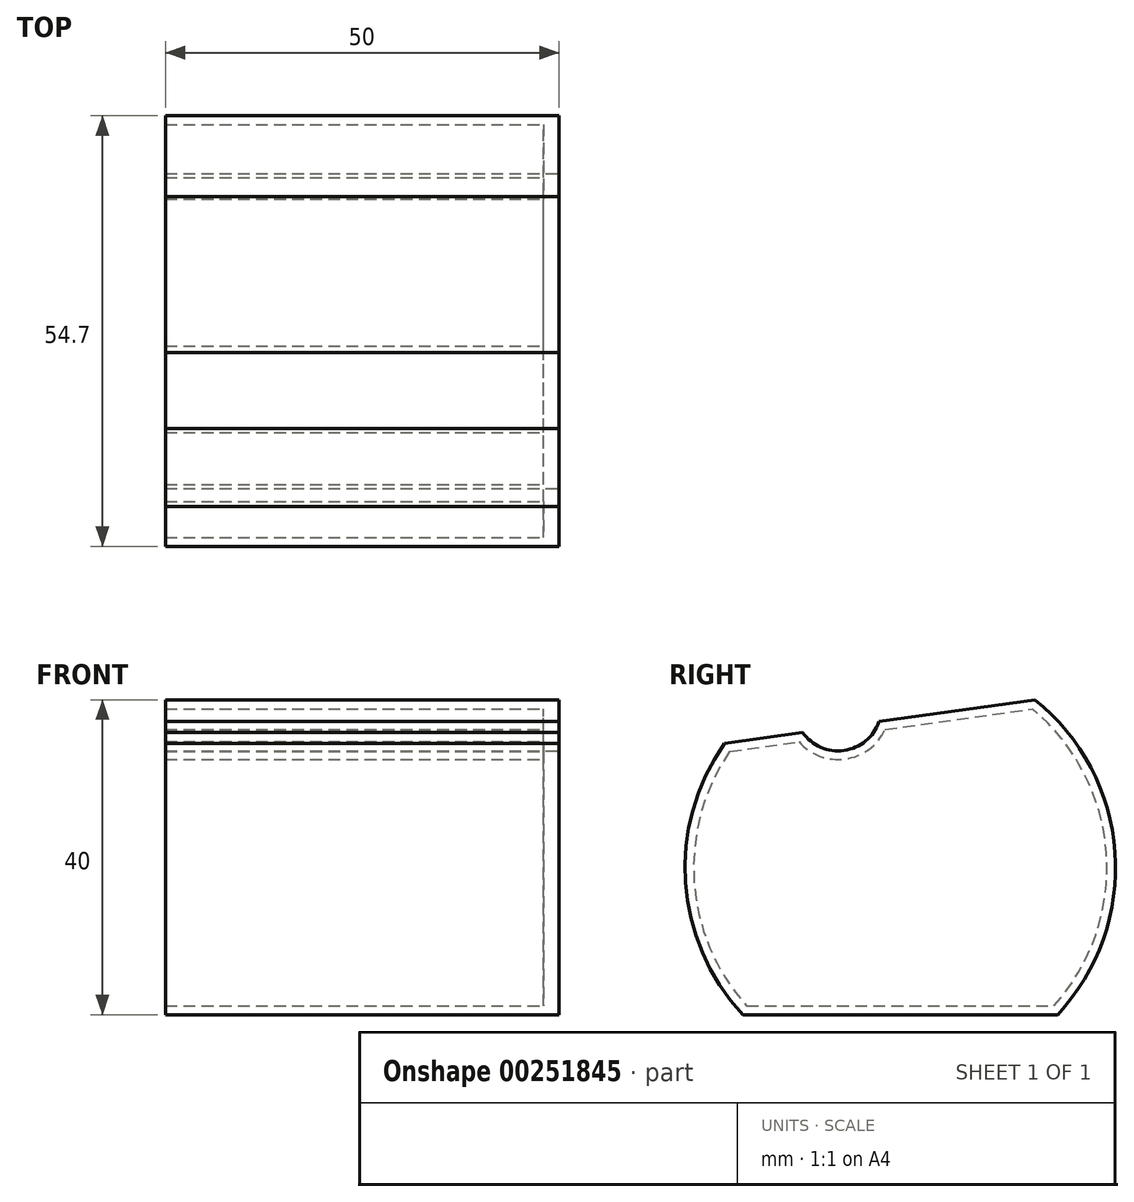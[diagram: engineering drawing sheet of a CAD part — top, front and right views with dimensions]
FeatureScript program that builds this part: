
annotation { "Feature Type Name" : "Feature", "Feature Type Description" : "" }
export const myFeature = defineFeature(function(context is Context, id is Id, definition is map)
    precondition{}
    {
        {
            var Q0;
            Q0=qCreatedBy(makeId("Right.planeOp"),FACE);
            var sketch = newSketch(context, id + "F0", { "sketchPlane" : qUnion([Q0])});
            skArc(sketch, "E0", {"start": v(21.5, -15.89) * mm, "mid": v(28.78, 4.75) * mm, "end": v(18.6, 24.11) * mm});
            skArc(sketch, "E1.trimOffspring", {"start": v(-20.82, 18.58) * mm, "mid": v(-25.79, 0.93) * mm, "end": v(-18.5, -15.89) * mm});
            skLineSegment(sketch, "E2", {"start": v(-20.82, 18.58) * mm, "end": v(-10.91, 19.97) * mm});
            skLineSegment(sketch, "E3.trimOffspring", {"start": v(25.8, -84.09) * mm, "end": v(25.8, -84.09) * mm});
            skLineSegment(sketch, "E4", {"start": v(-18.5, -15.89) * mm, "end": v(21.5, -15.89) * mm});
            skArc(sketch, "E5", {"start": v(-10.91, 19.97) * mm, "mid": v(-5.64, 17.68) * mm, "end": v(-1.21, 21.33) * mm});
            skLineSegment(sketch, "E6.trimOffspring", {"start": v(-1.21, 21.33) * mm, "end": v(18.6, 24.11) * mm});
            skLineSegment(sketch, "E7.0", {"start": v(-20.19, 17.55) * mm, "end": v(-11.39, 18.8) * mm});
            skLineSegment(sketch, "E7.1", {"start": v(-18.02, -14.79) * mm, "end": v(21.02, -14.79) * mm});
            skArc(sketch, "E7.2", {"start": v(21.02, -14.79) * mm, "mid": v(27.68, 4.67) * mm, "end": v(18.27, 22.96) * mm});
            skArc(sketch, "E7.3", {"start": v(-20.19, 17.55) * mm, "mid": v(-24.69, 1) * mm, "end": v(-18.02, -14.79) * mm});
            skLineSegment(sketch, "E7.4", {"start": v(-0.43, 20.33) * mm, "end": v(18.27, 22.96) * mm});
            skArc(sketch, "E7.5", {"start": v(-11.39, 18.8) * mm, "mid": v(-5.5, 16.59) * mm, "end": v(-0.43, 20.33) * mm});
            skSolve(sketch);
        }
        {
            var Q0;
            Q0=makeQuery(id+"F0.imprint","IMPRINT",FACE,{"disambiguationData":[TD([[makeQuery(id+"F0.imprint","IMPRINT",EDGE,{"derivedFrom":sQuery(id+"F0.wireOp",EDGE,"E0")}),1.0]])]});
            extrude(context, id + "F1", {"entities" : qUnion([Q0]), "oppositeDirection" : true, "depth" : 50 * mm});
        }
        {
            var Q0;
            Q0=makeQuery(id+"F0.imprint","IMPRINT",FACE,{"disambiguationData":[TD([[makeQuery(id+"F0.imprint","IMPRINT",EDGE,{"derivedFrom":sQuery(id+"F0.wireOp",EDGE,"E7.0")}),-1.0]])]});
            extrude(context, id + "F2", {"entities" : qUnion([Q0]), "operationType" : NewBodyOperationType.ADD, "oppositeDirection" : true, "depth" : 2 * mm});
        }
    });
